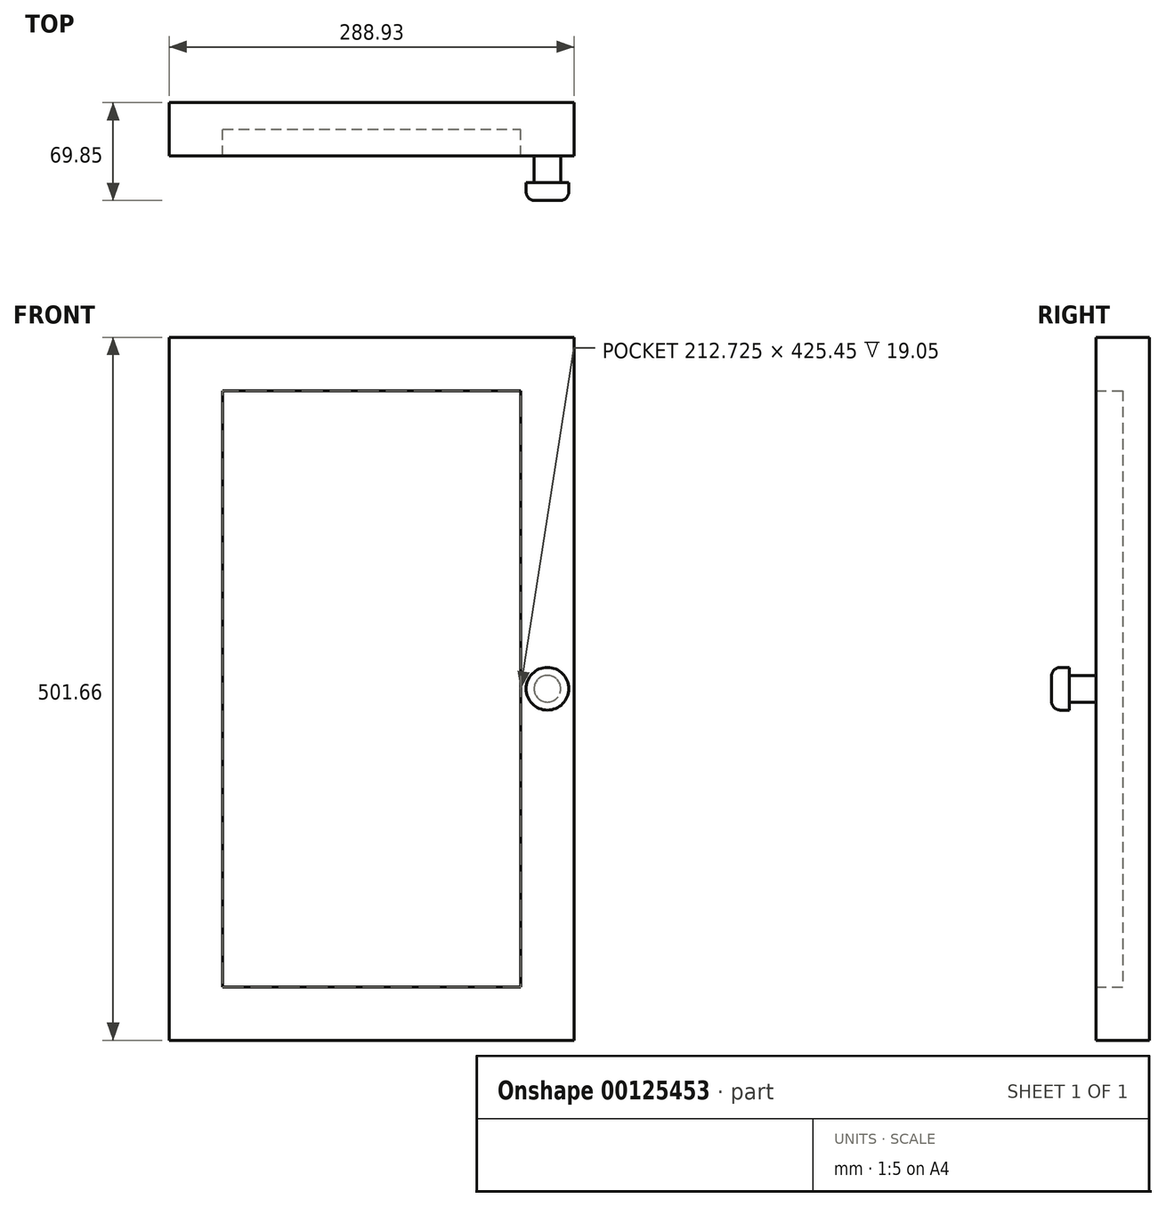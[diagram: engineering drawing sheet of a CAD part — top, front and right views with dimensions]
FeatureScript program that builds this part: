
annotation { "Feature Type Name" : "Feature", "Feature Type Description" : "" }
export const myFeature = defineFeature(function(context is Context, id is Id, definition is map)
    precondition{}
    {
        {
            var Q0;
            Q0=qCreatedBy(makeId("Front.planeOp"),FACE);
            var sketch = newSketch(context, id + "F0", { "sketchPlane" : qUnion([Q0])});
            skLineSegment(sketch, "E0.bottom", {"start": v(0, 250.83) * mm, "end": v(288.93, 250.83) * mm});
            skLineSegment(sketch, "E0.top", {"start": v(0, -250.83) * mm, "end": v(288.93, -250.83) * mm});
            skLineSegment(sketch, "E0.left", {"start": v(0, 250.83) * mm, "end": v(0, -250.83) * mm});
            skLineSegment(sketch, "E0.right", {"start": v(288.93, 250.83) * mm, "end": v(288.93, -250.83) * mm});
            skSolve(sketch);
        }
        {
            var Q0;
            Q0 = qSketchRegion(id + "F0", true);
            extrude(context, id + "F1", {"entities" : qUnion([Q0]), "depth" : 19.05 * mm});
        }
        {
            var Q0;
            Q0=makeQuery(id+"F1.opExtrude","CAP_FACE",FACE,{"disambiguationData":[OSD([sQuery(id+"F0.wireOp",EDGE,"E0.bottom"),sQuery(id+"F0.wireOp",EDGE,"E0.top"),sQuery(id+"F0.wireOp",EDGE,"E0.left"),sQuery(id+"F0.wireOp",EDGE,"E0.right")])],"isStart":false});
            var sketch = newSketch(context, id + "F2", { "sketchPlane" : qUnion([Q0])});
            skLineSegment(sketch, "E1.bottom", {"start": v(0, 250.83) * mm, "end": v(288.93, 250.83) * mm});
            skLineSegment(sketch, "E1.top", {"start": v(0, -250.83) * mm, "end": v(288.93, -250.83) * mm});
            skLineSegment(sketch, "E1.left", {"start": v(0, 250.83) * mm, "end": v(0, -250.83) * mm});
            skLineSegment(sketch, "E1.right", {"start": v(288.93, 250.83) * mm, "end": v(288.93, -250.83) * mm});
            skLineSegment(sketch, "E2.0", {"start": v(250.83, 212.72) * mm, "end": v(250.83, -212.72) * mm});
            skLineSegment(sketch, "E2.1", {"start": v(38.1, 212.72) * mm, "end": v(250.83, 212.72) * mm});
            skLineSegment(sketch, "E2.2", {"start": v(38.1, 212.72) * mm, "end": v(38.1, -212.72) * mm});
            skLineSegment(sketch, "E2.3", {"start": v(38.1, -212.72) * mm, "end": v(250.83, -212.72) * mm});
            skSolve(sketch);
        }
        {
            var Q0;
            Q0 = qSketchRegion(id + "F2", true);
            extrude(context, id + "F3", {"entities" : qUnion([Q0]), "operationType" : NewBodyOperationType.ADD, "depth" : 19.05 * mm});
        }
        {
            var Q0;
            Q0=qCreatedBy(makeId("Top.planeOp"),FACE);
            var sketch = newSketch(context, id + "F4", { "sketchPlane" : qUnion([Q0])});
            skLineSegment(sketch, "E3", {"start": v(269.88, 0) * mm, "end": v(269.88, -254) * mm, "construction": true});
            skLineSegment(sketch, "E4", {"start": v(0, 0) * mm, "end": v(288.93, 0) * mm, "construction": true});
            skLineSegment(sketch, "E5", {"start": v(279.4, 0) * mm, "end": v(279.4, -57.15) * mm});
            skLineSegment(sketch, "E6", {"start": v(279.4, -57.15) * mm, "end": v(285.12, -57.15) * mm});
            skLineSegment(sketch, "E7", {"start": v(285.12, -57.15) * mm, "end": v(285.12, -63.5) * mm});
            skLineSegment(sketch, "E8", {"start": v(278.76, -69.85) * mm, "end": v(269.87, -69.85) * mm});
            skPoint(sketch, "E9.visualSharp", {"position": v(285.11, -69.85) * mm});
            skArc(sketch, "E9.filletArc", {"start": v(278.76, -69.85) * mm, "mid": v(283.26, -68) * mm, "end": v(285.12, -63.5) * mm});
            skLineSegment(sketch, "E10", {"start": v(279.4, 0) * mm, "end": v(269.88, 0) * mm});
            skLineSegment(sketch, "E11", {"start": v(269.88, 0) * mm, "end": v(269.88, -69.85) * mm});
            skSolve(sketch);
        }
        {
            var Q0;
            Q0=makeQuery(id+"F4.imprint","IMPRINT",FACE,{"disambiguationData":[TD([[makeQuery(id+"F4.imprint","IMPRINT",EDGE,{"derivedFrom":sQuery(id+"F4.wireOp",EDGE,"E5")}),-1.0]])]});
            var Q1;
            Q1=sQuery(id+"F4.wireOp",EDGE,"E3");
            revolve(context, id + "F5", {"operationType" : NewBodyOperationType.ADD, "entities" : qUnion([Q0]), "axis" : qUnion([Q1]), "revolveType" : RevolveType.FULL});
        }
    });
